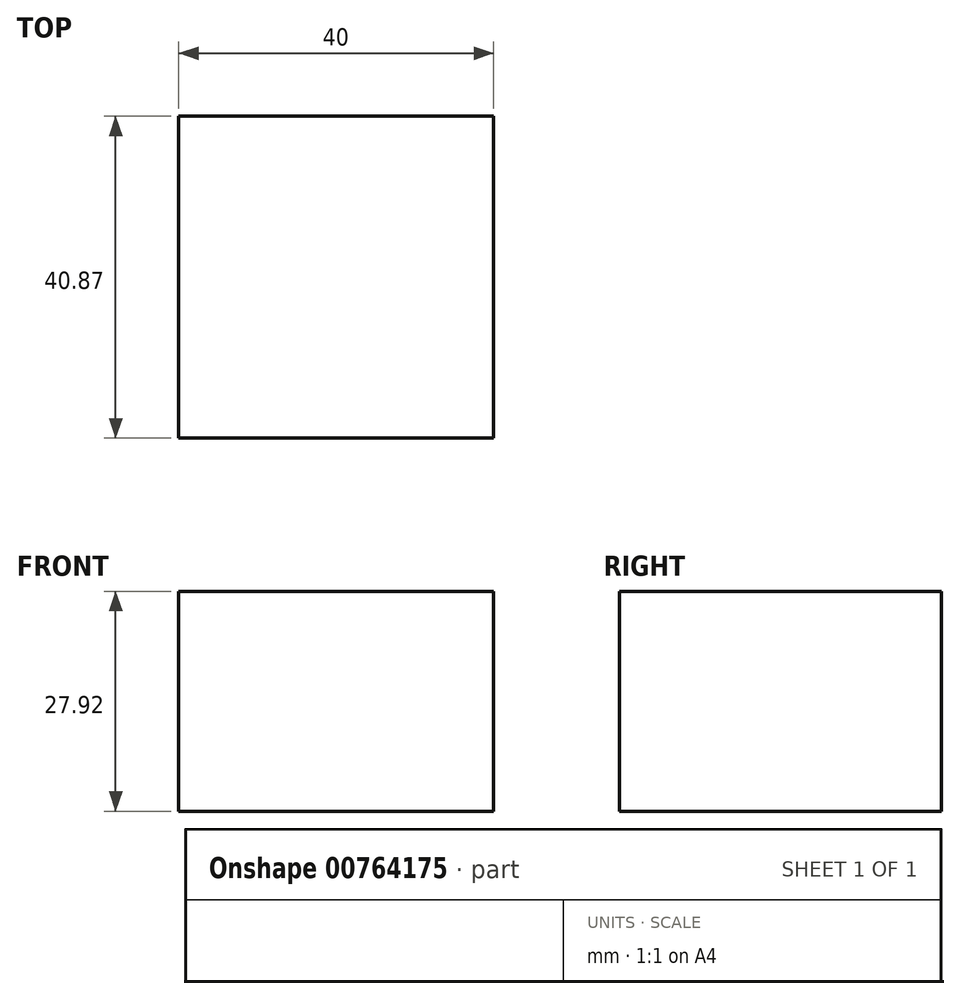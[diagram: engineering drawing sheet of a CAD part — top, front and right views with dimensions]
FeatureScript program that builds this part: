
annotation { "Feature Type Name" : "Feature", "Feature Type Description" : "" }
export const myFeature = defineFeature(function(context is Context, id is Id, definition is map)
    precondition{}
    {
        {
            var Q0;
            Q0=qCreatedBy(makeId("Right.planeOp"),FACE);
            var sketch = newSketch(context, id + "F0", { "sketchPlane" : qUnion([Q0])});
            skLineSegment(sketch, "E0.bottom", {"start": v(-9.84, 18.57) * mm, "end": v(31.03, 18.57) * mm});
            skLineSegment(sketch, "E0.top", {"start": v(-9.84, -9.35) * mm, "end": v(31.03, -9.35) * mm});
            skLineSegment(sketch, "E0.left", {"start": v(-9.84, 18.57) * mm, "end": v(-9.84, -9.35) * mm});
            skLineSegment(sketch, "E0.right", {"start": v(31.03, 18.57) * mm, "end": v(31.03, -9.35) * mm});
            skSolve(sketch);
        }
        {
            var Q0;
            Q0 = qSketchRegion(id + "F0", true);
            extrude(context, id + "F1", {"entities" : qUnion([Q0]), "depth" : 40 * mm, "offsetDistance" : 25 * mm});
        }
    });
